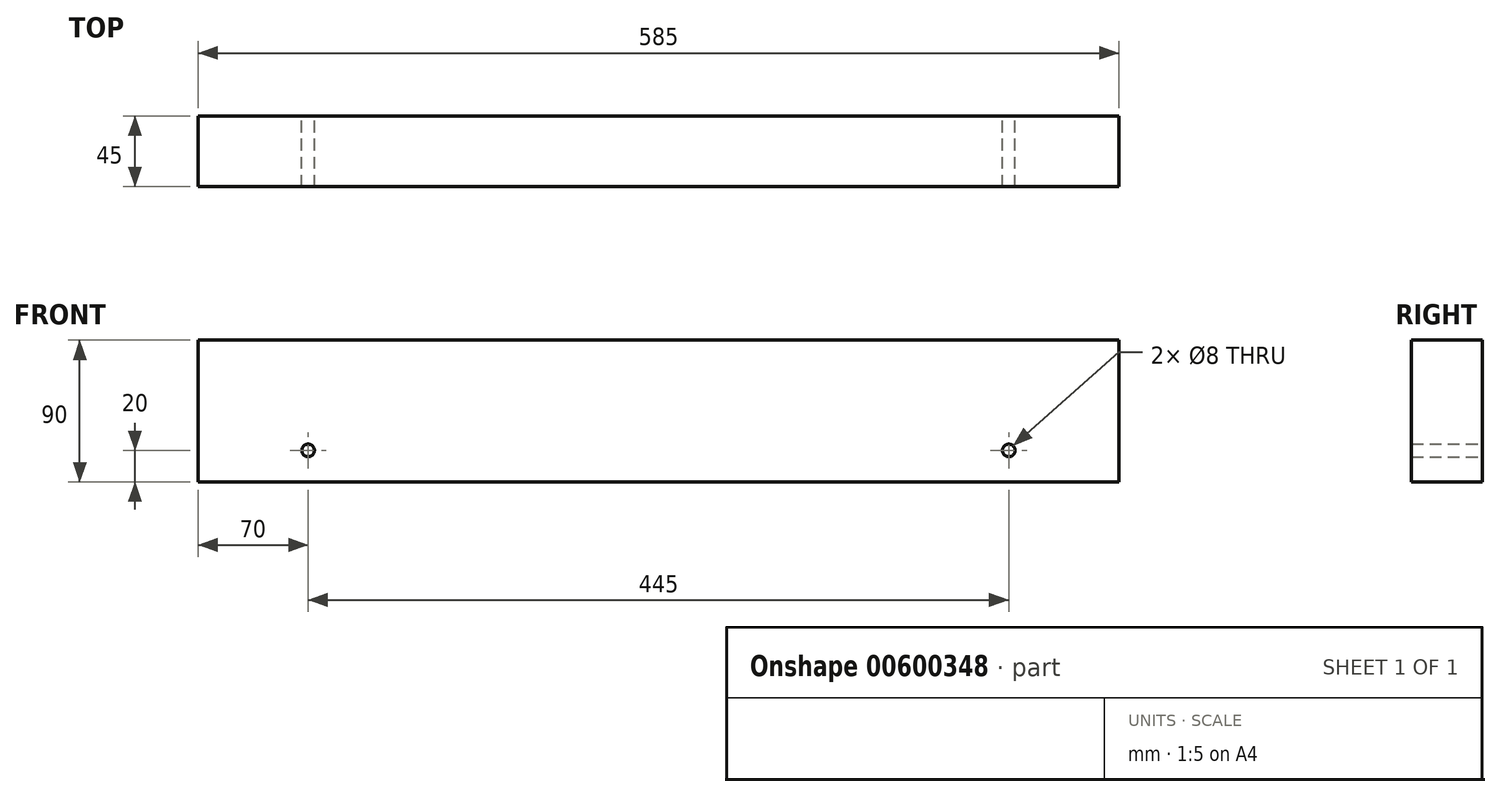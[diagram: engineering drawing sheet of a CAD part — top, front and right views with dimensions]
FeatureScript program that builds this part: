
annotation { "Feature Type Name" : "Feature", "Feature Type Description" : "" }
export const myFeature = defineFeature(function(context is Context, id is Id, definition is map)
    precondition{}
    {
        {
            var Q0;
            Q0=qCreatedBy(makeId("Front.planeOp"),FACE);
            var sketch = newSketch(context, id + "F0", { "sketchPlane" : qUnion([Q0])});
            skLineSegment(sketch, "E0.bottom", {"start": v(-292.5, 442.5) * mm, "end": v(292.5, 442.5) * mm});
            skLineSegment(sketch, "E0.top", {"start": v(-292.5, 532.5) * mm, "end": v(292.5, 532.5) * mm});
            skLineSegment(sketch, "E0.left", {"start": v(-292.5, 442.5) * mm, "end": v(-292.5, 532.5) * mm});
            skLineSegment(sketch, "E0.right", {"start": v(292.5, 442.5) * mm, "end": v(292.5, 532.5) * mm});
            skLineSegment(sketch, "E1.bottom", {"start": v(-292.5, 442.5) * mm, "end": v(-202.5, 442.5) * mm});
            skLineSegment(sketch, "E1.top", {"start": v(-292.5, -442.5) * mm, "end": v(-202.5, -442.5) * mm});
            skLineSegment(sketch, "E1.left", {"start": v(-292.5, 442.5) * mm, "end": v(-292.5, -442.5) * mm});
            skLineSegment(sketch, "E1.right", {"start": v(-202.5, 442.5) * mm, "end": v(-202.5, -442.5) * mm});
            skLineSegment(sketch, "E2.bottom", {"start": v(-292.5, -442.5) * mm, "end": v(292.5, -442.5) * mm});
            skLineSegment(sketch, "E2.top", {"start": v(-292.5, -532.5) * mm, "end": v(292.5, -532.5) * mm});
            skLineSegment(sketch, "E2.left", {"start": v(-292.5, -442.5) * mm, "end": v(-292.5, -532.5) * mm});
            skLineSegment(sketch, "E2.right", {"start": v(292.5, -442.5) * mm, "end": v(292.5, -532.5) * mm});
            skLineSegment(sketch, "E3.bottom", {"start": v(292.5, -442.5) * mm, "end": v(202.5, -442.5) * mm});
            skLineSegment(sketch, "E3.top", {"start": v(292.5, 442.5) * mm, "end": v(202.5, 442.5) * mm});
            skLineSegment(sketch, "E3.left", {"start": v(292.5, -442.5) * mm, "end": v(292.5, 442.5) * mm});
            skLineSegment(sketch, "E3.right", {"start": v(202.5, -442.5) * mm, "end": v(202.5, 442.5) * mm});
            skLineSegment(sketch, "E4.0", {"start": v(-292.5, 472.5) * mm, "end": v(292.5, 472.5) * mm, "construction": true});
            skLineSegment(sketch, "E5.0", {"start": v(232.5, -442.5) * mm, "end": v(232.5, 442.5) * mm, "construction": true});
            skLineSegment(sketch, "E6.0", {"start": v(-292.5, -472.5) * mm, "end": v(292.5, -472.5) * mm, "construction": true});
            skLineSegment(sketch, "E7.0", {"start": v(-232.5, 442.5) * mm, "end": v(-232.5, -442.5) * mm, "construction": true});
            skLineSegment(sketch, "E8", {"start": v(232.5, 442.5) * mm, "end": v(232.5, 472.5) * mm, "construction": true});
            skLineSegment(sketch, "E9", {"start": v(-232.5, 442.5) * mm, "end": v(-232.5, 472.5) * mm, "construction": true});
            skLineSegment(sketch, "E10", {"start": v(232.5, -442.5) * mm, "end": v(232.5, -472.5) * mm, "construction": true});
            skLineSegment(sketch, "E11", {"start": v(-232.5, -442.5) * mm, "end": v(-232.5, -472.5) * mm, "construction": true});
            skLineSegment(sketch, "E12.0", {"start": v(222.5, 442.5) * mm, "end": v(222.5, 472.5) * mm, "construction": true});
            skLineSegment(sketch, "E13.0", {"start": v(-292.5, 462.5) * mm, "end": v(292.5, 462.5) * mm, "construction": true});
            skCircle(sketch, "E14", {"center": v(222.5, 462.5) * mm, "radius": 4 * mm});
            skLineSegment(sketch, "E15.0", {"start": v(-222.5, 442.5) * mm, "end": v(-222.5, 472.5) * mm, "construction": true});
            skCircle(sketch, "E16", {"center": v(-222.5, 462.5) * mm, "radius": 4 * mm});
            skLineSegment(sketch, "E17.0", {"start": v(222.5, -442.5) * mm, "end": v(222.5, -472.5) * mm, "construction": true});
            skLineSegment(sketch, "E18.0", {"start": v(-292.5, -462.5) * mm, "end": v(292.5, -462.5) * mm, "construction": true});
            skLineSegment(sketch, "E19.0", {"start": v(-222.5, -442.5) * mm, "end": v(-222.5, -472.5) * mm, "construction": true});
            skCircle(sketch, "E20", {"center": v(-222.5, -462.5) * mm, "radius": 4 * mm});
            skCircle(sketch, "E21", {"center": v(222.5, -462.5) * mm, "radius": 4 * mm});
            skSolve(sketch);
        }
        {
            var Q0;
            Q0=makeQuery(id+"F0.imprint","IMPRINT",FACE,{"disambiguationData":[TD([[makeQuery(id+"F0.imprint","IMPRINT",EDGE,{"derivedFrom":sQuery(id+"F0.wireOp",EDGE,"E0.bottom")}),1.0]])]});
            extrude(context, id + "F1", {"entities" : qUnion([Q0]), "depth" : 45 * mm, "offsetDistance" : 25 * mm});
        }
    });
